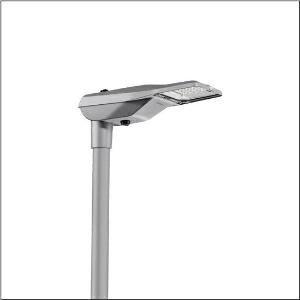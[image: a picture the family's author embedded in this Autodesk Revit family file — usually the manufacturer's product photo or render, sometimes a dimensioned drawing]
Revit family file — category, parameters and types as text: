
# Revit family: streetlight_sl_21_iq_micro___st1_0a_5xe1d21y08cb_9119
name_source: partatom
category: Lighting Fixtures
units: mm (PartAtom-declared; Revit-internal decimal feet)

## family parameters
Cut with Voids When Loaded = No
Host = Face
Light Source = No
Part Type = Normal
Room Calculation Point = No
Round Connector Dimension = Use Diameter
Shared = No

## types (1)
- --- (1 x LED, 2310 lm, 19.1 W, 2200K)
    Apparent Load = 19 VA
    CIE Flux Codes = 37 72 97 100 100
    Color Rendering = 70
    Color Temperature = 2200K
    Default Elevation = 1800 mm
    Description = Streetlight SL 21 iQ micro, mast luminaire, primary light control with lens, of PMMA, primary optical cover: cover, of toughened safety glass, transparent, light distribution: ST1.0a, light emission: direct distribution, primary light characteristic: asymmetric, installation type: post-top, side-entry, LED, High Power LED, rated luminous flux: 2.310lm, luminous efficacy: 121lm/W, light colour: 722, colour temperature: 2200K, control: presetting dimming logarithmic, Street-Remote, Auto-Match, Temp-Guard, Lumen-Switch, Night-Set, Smart-Wire, Light-Fading, Desk-Remote (wireless, voltage-free reading and setting of iQ features in the workshop via application-optimized NFC function/RFID function), optimised constant luminous flux control (CLO 2.0), mains connection: 220..240V, AC, 50/60Hz, start of lifetime: 19W, end of service life: 20W, reduction: 9W, luminaire housing, of diecast aluminium, powder-coated, Siteco® metallic grey (DB 702S), corrosivity category C5 mid according to DIN EN ISO 12944, please order mast flange separately, inclination adjustable: 0°, 5°, 10°, 15°, sealing non-destructively replaceable, multi-level sealing system, length: 528mm, width: 235mm, height: 110mm, mast flange for spigot size: 42mm (side-entry): 5XC10008XM4, 60/48mm (side-entry/post-top): 5XC10108XM2, 76/60mm (side-entry/post-top): 5XC10108XM1, Smart Interface below and above, protection rating (complete): IP66, insulation class (complete): insulation class II (safety insulation), certification: CE, ENEC, ENEC+, VDE, impact resistance: IK09, permissible operating ambient temperature for outdoor applications: -40..+50°C, standard-compliant lighting for roads and squares, packaging unit: 1 piece

Light Distribution: ST1.0a
    Height = 110 mm
    Lamp = 1 x LED
    Lamp Light Flux = 2310 lm
    Lamp Power = 19.1 W
    Lamp count = 1
    Length = 528 mm
    Luminous efficacy = 121 lm/W
    Manufacturer = Siteco
    ModVariant = No
    Model = 5XE1D21Y08CB
    Number of Poles = 1
    OnlyDefault = Yes
    Power Factor = 1
    Product Name = Streetlight SL 21 iQ micro | ST1.0a
    Product group = mast luminaire | pylon top
    ProductGroupID = 6100
    Protection Class = Protection class II
    Protection Degree = IP 66
    RLX_Detail_Level = 1
    RLX_Emergency_Light_Flux = 0 lm
    RLX_Emergency_Type = 0
    RLX_Emergency_Type_DB = No
    RlxData = <blob elided: 98693 chars, md5=d8192ab6>
    Socket = socket
    Standby Power = 0 W
    System Light Flux = 2310 lm
    System Power = 19 W
    Type Comments = factory setting: luminous flux: 100 % | dim-lin: 254 | 387 mA
    Type Image = l_1007239.jpg
    URL = http://relux.com
    VarID = @adj_063805
    Voltage = 0 V
    Weight = 0.00 kg
    Width = 235 mm

## geometry (parser evidence)
native form markers: Blend x4, Sweep x11
no freeform markers — native parametric forms only
